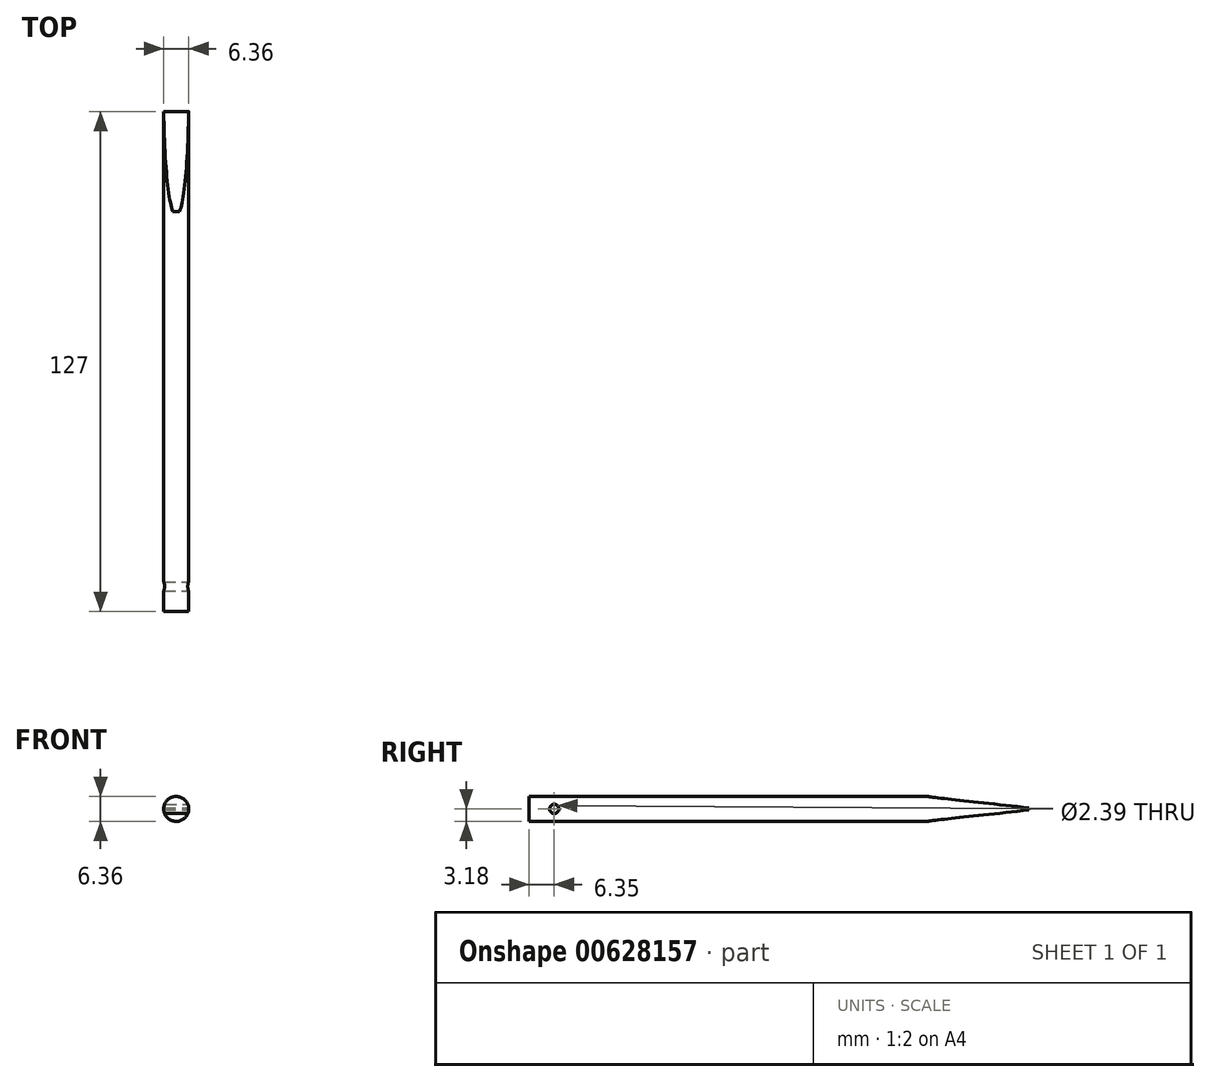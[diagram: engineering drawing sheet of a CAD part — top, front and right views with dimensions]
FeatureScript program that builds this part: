
annotation { "Feature Type Name" : "Feature", "Feature Type Description" : "" }
export const myFeature = defineFeature(function(context is Context, id is Id, definition is map)
    precondition{}
    {
        {
            var Q0;
            Q0=qCreatedBy(makeId("Front.planeOp"),FACE);
            var sketch = newSketch(context, id + "F0", { "sketchPlane" : qUnion([Q0])});
            skCircle(sketch, "E0", {"center": v(0, 0) * mm, "radius": 3.18 * mm});
            skSolve(sketch);
        }
        {
            var Q0;
            Q0 = qSketchRegion(id + "F0", true);
            extrude(context, id + "F1", {"entities" : qUnion([Q0]), "depth" : 127 * mm, "offsetDistance" : 25.4 * mm});
        }
        {
            var Q0;
            Q0=qCreatedBy(makeId("Right.planeOp"),FACE);
            var sketch = newSketch(context, id + "F2", { "sketchPlane" : qUnion([Q0])});
            skCircle(sketch, "E1", {"center": v(-120.65, 0) * mm, "radius": 1.2 * mm});
            skLineSegment(sketch, "E2", {"start": v(-128.62, 0) * mm, "end": v(2, 0) * mm, "construction": true});
            skLineSegment(sketch, "E3", {"start": v(0, -3.06) * mm, "end": v(0, -0.26) * mm});
            skLineSegment(sketch, "E4.MirrorCS", {"start": v(0, 3.06) * mm, "end": v(0, 0.26) * mm});
            skLineSegment(sketch, "E5", {"start": v(-25.4, 3.06) * mm, "end": v(0, 0.26) * mm});
            skLineSegment(sketch, "E6", {"start": v(-25.4, -3.06) * mm, "end": v(0, -0.26) * mm});
            skLineSegment(sketch, "E7", {"start": v(-25.4, 3.06) * mm, "end": v(-25.4, 8) * mm});
            skLineSegment(sketch, "E8", {"start": v(-25.4, 8) * mm, "end": v(0, 8) * mm});
            skLineSegment(sketch, "E9", {"start": v(0, 8) * mm, "end": v(0, 3.06) * mm});
            skLineSegment(sketch, "E10", {"start": v(-25.4, -3.06) * mm, "end": v(-25.4, -7.65) * mm});
            skLineSegment(sketch, "E11", {"start": v(-25.4, -7.65) * mm, "end": v(0, -7.65) * mm});
            skLineSegment(sketch, "E12", {"start": v(0, -7.65) * mm, "end": v(0, -3.06) * mm});
            skPoint(sketch, "E13.MirrorCS.start.orphan", {"position": v(0, -3.06) * mm});
            skSolve(sketch);
        }
        {
            var Q0;
            Q0 = qSketchRegion(id + "F2", true);
            extrude(context, id + "F3", {"entities" : qUnion([Q0]), "operationType" : NewBodyOperationType.REMOVE, "endBound" : BoundingType.SYMMETRIC, "oppositeDirection" : true, "depth" : 25.4 * mm, "offsetDistance" : 25.4 * mm});
        }
    });
